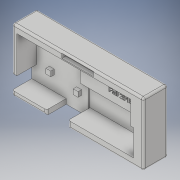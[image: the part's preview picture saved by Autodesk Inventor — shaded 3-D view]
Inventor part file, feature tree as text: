
AUTODESK INVENTOR PART (.ipt)
format: ipt  version: 2017 (Build 210142000, 142)  size: 497,664 bytes
history: native  units: in
note: dims shown in document units (in); Inventor stores cm internally (conversion verified against a paired STEP export)
features: extrude x9, sketch x9, fillet x2
ambient origin geometry x8: Origin, YZ Plane, XZ Plane, XY Plane, X Axis, Y Axis, Z Axis, Center Point
bodies: Solid1 (feature_tree)
feature tree (20):
  extrude  "Extrusion1"  Depth=2.5197in
  extrude  "Extrusion2"  Depth=0.9843in
  extrude  "Extrusion3"  Depth=0.7874in TaperAngle=0.0deg
  extrude  "Extrusion4"  Depth=1.0433in
  extrude  "Extrusion5"  Depth=0.5118in
  extrude  "Extrusion6"  Depth=0.9843in
  extrude  "Extrusion7"  Depth=1.9685in
  extrude  "Extrusion8"  Depth=0.1181in
  extrude  "Extrusion9"  Depth=0.0787in
  fillet  "Fillet1"  Radius=0.563in
  fillet  "Fillet3"  Radius=0.4921in
  sketch  "Sketch1"  dims[d0=5.2362in d1=2.5197in]
  sketch  "Sketch2"  dims[d2=0.9843in d3=0.0in d10=2.0472in]
  sketch  "Sketch3"  dims[d11=2.0472in d12=0.7874in d13=0.0in]
  sketch  "Sketch4"  dims[d15=2.5984in d16=1.0433in]
  sketch  "Sketch5"  dims[d17=0.8661in d18=0.0in d19=0.5118in]
  sketch  "Sketch6"  dims[d20=0.9843in d21=0.0in d22=2.4803in]
  sketch  "Sketch7"  dims[d23=0.4724in d24=0.0in d25=1.9685in]
  sketch  "Sketch8"  dims[d26=1.9685in d27=0.1181in]
  sketch  "Sketch9"  dims[d28=0.1732in d29=0.6575in d30=0.563in d31=0.4921in d32=0.3189in d33=0.1969in d34=0.1969in d35=0.1969in d36=0.1969in d37=0.1969in d38=0.1969in d39=0.1378in d40=0.0in d41=0.8661in d42=0.5906in d43=0.7874in d44=0.0in d49=1.2598in d50=0.1575in d51=0.0in d52=0.0591in d53=0.0in d54=0.0787in d56=0.0787in]
